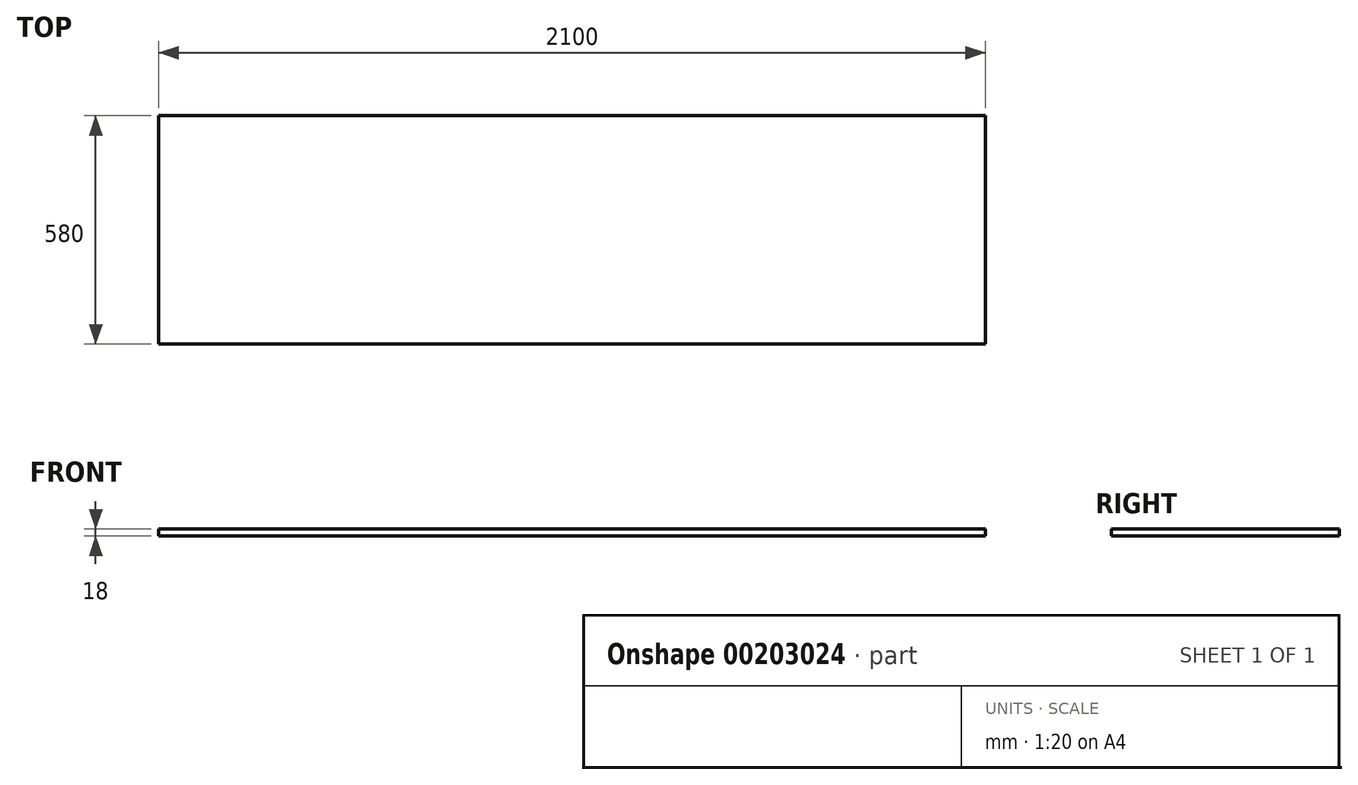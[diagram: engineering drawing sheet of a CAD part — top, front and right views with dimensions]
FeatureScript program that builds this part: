
annotation { "Feature Type Name" : "Feature", "Feature Type Description" : "" }
export const myFeature = defineFeature(function(context is Context, id is Id, definition is map)
    precondition{}
    {
        {
            var Q0;
            Q0=qCreatedBy(makeId("Top.planeOp"),FACE);
            var sketch = newSketch(context, id + "F0", { "sketchPlane" : qUnion([Q0])});
            skLineSegment(sketch, "E0.bottom", {"start": v(-1050, -290) * mm, "end": v(1050, -290) * mm});
            skLineSegment(sketch, "E0.top", {"start": v(-1050, 290) * mm, "end": v(1050, 290) * mm});
            skLineSegment(sketch, "E0.left", {"start": v(-1050, -290) * mm, "end": v(-1050, 290) * mm});
            skLineSegment(sketch, "E0.right", {"start": v(1050, -290) * mm, "end": v(1050, 290) * mm});
            skPoint(sketch, "E0.middle", {"position": v(0, 0) * mm});
            skSolve(sketch);
        }
        {
            var Q0;
            Q0=makeQuery(id+"F0.imprint","IMPRINT",FACE,{"disambiguationData":[TD([[makeQuery(id+"F0.imprint","IMPRINT",EDGE,{"derivedFrom":sQuery(id+"F0.wireOp",EDGE,"E0.bottom")}),1.0]])]});
            extrude(context, id + "F1", {"entities" : qUnion([Q0]), "depth" : 18 * mm});
        }
    });
